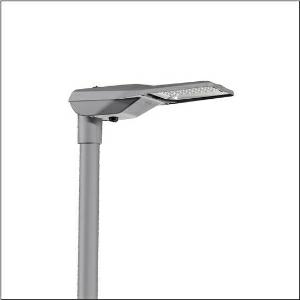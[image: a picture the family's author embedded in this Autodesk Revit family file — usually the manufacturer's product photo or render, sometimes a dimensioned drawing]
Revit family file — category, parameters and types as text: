
# Revit family: streetlight_sl_21_mini___st1_0a_5xe2d33t08gb_6341
name_source: partatom
category: Lighting Fixtures
units: mm (PartAtom-declared; Revit-internal decimal feet)

## family parameters
Cut with Voids When Loaded = No
Host = Face
Light Source = No
Part Type = Normal
Room Calculation Point = No
Round Connector Dimension = Use Diameter
Shared = No

## types (1)
- --- (1 x LED, 5940 lm, 40.4 W, 3000K)
    Apparent Load = 40 VA
    CIE Flux Codes = 37 72 97 100 100
    Color Rendering = 70
    Color Temperature = 3000K
    Default Elevation = 1800 mm
    Description = Streetlight SL 21 mini, mast luminaire, primary light control with lens, of PMMA, primary optical cover: cover, of toughened safety glass, transparent, light distribution: ST1.0a, light emission: direct distribution, primary light characteristic: asymmetric, installation type: side-entry, post-top, LED, High Power LED, rated luminous flux: 5.940lm, luminous efficacy: 147lm/W, light colour: 730, colour temperature: 3000K, control gear: D4i, control: flexible luminous flux parameterisation, time-dependent luminous flux control, constant luminous flux control, overheat protection, pre-setting: logarithmic dimming characteristic, mains connection: 220..240V, AC, 50/60Hz, start of lifetime: 40W, end of service life: 41W, reduction: 19W, luminaire housing, of diecast aluminium, powder-coated, SITECO metallic grey (DB 702S), corrosivity category C5 high according to DIN EN ISO 12944, please order mast flange separately, inclination adjustable: 0°, 5°, 10°, 15°, sealing non-destructively replaceable, multi-level sealing system, length: 628mm, width: 235mm, height: 110mm, mast flange for spigot size: 42mm (side-entry): 5XC10008XM4, 60/48mm (side-entry/post-top): 5XC10108XM2, 76/60mm (side-entry/post-top): 5XC10108XM1, mounting height: 4..8m, Smart Interface below and above, protection rating (complete): IP66, insulation class (complete): insulation class II (safety insulation), certification: CE, ENEC, ENEC+, VDE, impact resistance: IK10, permissible operating ambient temperature for outdoor applications: -40..+50°C, standard-compliant lighting for roads and squares, packaging unit: 1 piece

Light Distribution: ST1.0a
    Height = 110 mm
    Lamp = 1 x LED
    Lamp Light Flux = 5940 lm
    Lamp Power = 40.4 W
    Lamp count = 1
    Length = 625 mm
    Luminous efficacy = 147 lm/W
    Manufacturer = Siteco
    ModVariant = No
    Model = 5XE2D33T08GB
    Number of Poles = 1
    OnlyDefault = Yes
    Power Factor = 1
    Product Name = Streetlight SL 21 mini | ST1.0a
    Product group = mast luminaire | pylon top
    ProductGroupID = 6100
    Protection Class = Protection class II
    Protection Degree = IP 66
    RLX_Detail_Level = 1
    RLX_Emergency_Light_Flux = 0 lm
    RLX_Emergency_Type = 0
    RLX_Emergency_Type_DB = No
    RlxData = <blob elided: 26265 chars, md5=d51f37b8>
    Socket = socket
    Standby Power = 0 W
    System Light Flux = 5940 lm
    System Power = 40 W
    Type Comments = factory setting: luminous flux: 100 % | dim-lin: 254 | 812 mA
    Type Image = l_1003514.jpg
    URL = http://relux.com
    VarID = @adj_186045
    Voltage = 0 V
    Weight = 0.00 kg
    Width = 234 mm

## geometry (parser evidence)
native form markers: Blend x4, Sweep x8
no freeform markers — native parametric forms only
